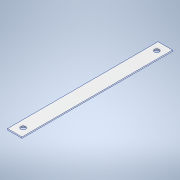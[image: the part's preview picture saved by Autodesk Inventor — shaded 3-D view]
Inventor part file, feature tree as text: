
AUTODESK INVENTOR PART (.ipt)
format: ipt  version: 2020 (Build 240168000, 168)  size: 113,664 bytes
history: native  units: mm
features: extrude x1, sketch x1
ambient origin geometry x8: Origin, YZ Plane, XZ Plane, XY Plane, X Axis, Y Axis, Z Axis, Center Point
bodies: Solid1 (feature_tree)
feature tree (2):
  extrude  "Extrusion1"  Depth=125.0mm
  sketch  "Sketch1"  dims[d0=12.0mm d1=125.0mm d2=4.0mm d6=7.0mm d7=6.0mm d10=1.0mm d11=0.0mm d36=4.0mm d37=111.0mm d38=7.0mm d39=55.5mm]
